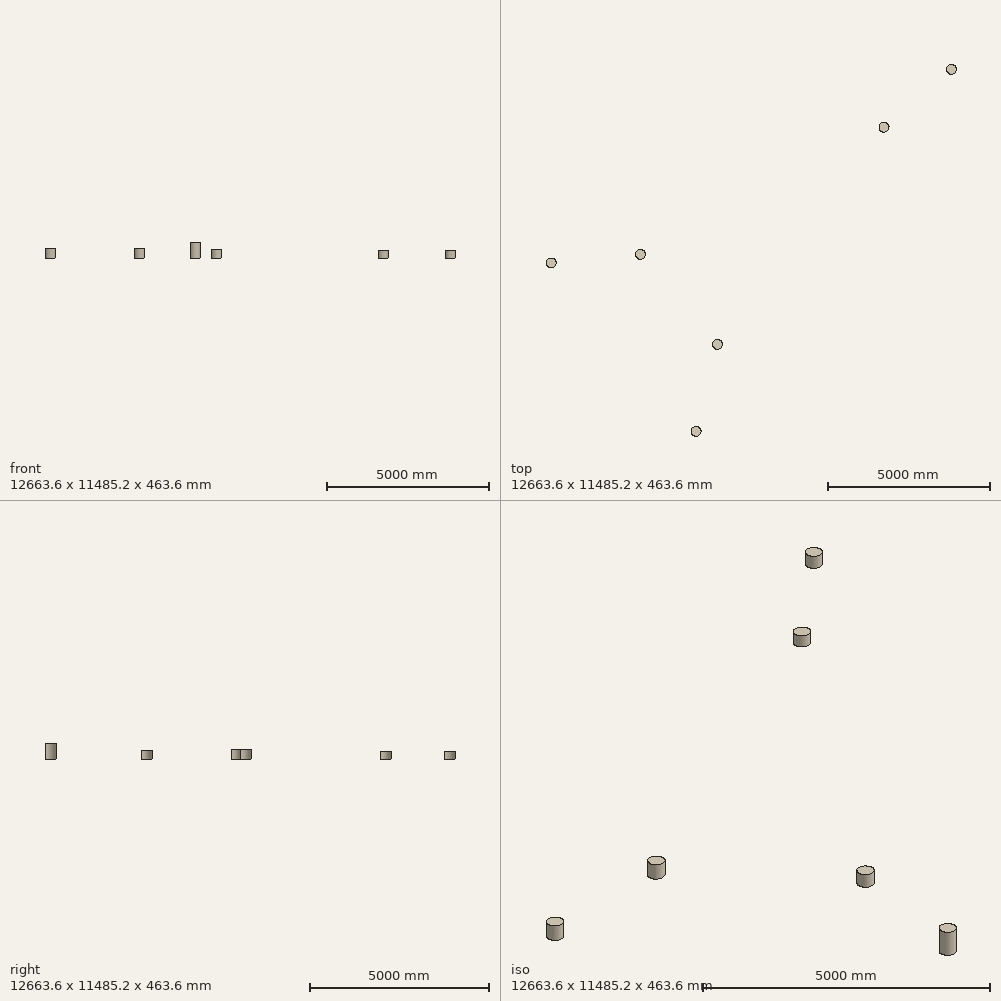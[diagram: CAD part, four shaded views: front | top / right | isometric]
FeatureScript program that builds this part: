
annotation { "Feature Type Name" : "Feature", "Feature Type Description" : "" }
export const myFeature = defineFeature(function(context is Context, id is Id, definition is map)
    precondition{}
    {
        {
            var Q0;
            Q0=qCreatedBy(makeId("Top.planeOp"),FACE);
            var sketch = newSketch(context, id + "F0", { "sketchPlane" : qUnion([Q0])});
            skLineSegment(sketch, "E0", {"start": v(5410.77, 4576.95) * mm, "end": v(-2479.54, -6603.46) * mm, "construction": true});
            skLineSegment(sketch, "E1", {"start": v(-2479.54, -6603.46) * mm, "end": v(-6948.04, -1401.09) * mm, "construction": true});
            skLineSegment(sketch, "E2", {"start": v(-6948.04, -1401.09) * mm, "end": v(5410.77, 4576.95) * mm, "construction": true});
            skLineSegment(sketch, "E3", {"start": v(5410.77, 4576.95) * mm, "end": v(-1814.73, -3915.86) * mm, "construction": true});
            skLineSegment(sketch, "E4", {"start": v(-1814.73, -3915.86) * mm, "end": v(-2479.54, -6603.46) * mm, "construction": true});
            skLineSegment(sketch, "E5", {"start": v(-1814.73, -3915.86) * mm, "end": v(-6948.04, -1401.09) * mm, "construction": true});
            skLineSegment(sketch, "E6", {"start": v(-1814.73, -3915.86) * mm, "end": v(-4192.13, -1136.3) * mm, "construction": true});
            skLineSegment(sketch, "E7", {"start": v(-4192.13, -1136.3) * mm, "end": v(-6948.04, -1401.09) * mm, "construction": true});
            skLineSegment(sketch, "E8", {"start": v(-4192.13, -1136.3) * mm, "end": v(-2479.54, -6603.46) * mm, "construction": true});
            skLineSegment(sketch, "E9", {"start": v(-4192.13, -1136.3) * mm, "end": v(3327.24, 2791.88) * mm, "construction": true});
            skLineSegment(sketch, "E10", {"start": v(3327.24, 2791.88) * mm, "end": v(-1814.73, -3915.86) * mm, "construction": true});
            skLineSegment(sketch, "E11", {"start": v(0, 0) * mm, "end": v(3327.24, 2791.88) * mm, "construction": true});
            skCircle(sketch, "E12", {"center": v(0, 0) * mm, "radius": 4343.4 * mm, "construction": true});
            skLineSegment(sketch, "E13", {"start": v(0, 0) * mm, "end": v(0, 9025.7) * mm});
            skCircle(sketch, "E14", {"center": v(0, 0) * mm, "radius": 7061.2 * mm, "construction": true});
            skCircle(sketch, "E15", {"center": v(0, 0) * mm, "radius": 4953 * mm, "construction": true});
            skLineSegment(sketch, "E16", {"start": v(3327.24, 2791.88) * mm, "end": v(4675.95, 1633.32) * mm, "construction": true});
            skLineSegment(sketch, "E17", {"start": v(4675.95, 1633.32) * mm, "end": v(4675.95, 1633.32) * mm});
            skSolve(sketch);
        }
        {
            var Q0;
            Q0=qCreatedBy(makeId("Top.planeOp"),FACE);
            var sketch = newSketch(context, id + "F1", { "sketchPlane" : qUnion([Q0])});
            skCircle(sketch, "E18", {"center": v(5410.77, 4576.95) * mm, "radius": 152.4 * mm});
            skSolve(sketch);
        }
        {
            var Q0;
            Q0=qSketchRegion(id+"F1",true);
            extrude(context, id + "F2", {"entities" : qUnion([Q0]), "depth" : 241.3 * mm});
        }
        {
            var Q0;
            Q0=qCreatedBy(makeId("Top.planeOp"),FACE);
            var sketch = newSketch(context, id + "F3", { "sketchPlane" : qUnion([Q0])});
            skCircle(sketch, "E19", {"center": v(3327.24, 2791.88) * mm, "radius": 152.4 * mm});
            skSolve(sketch);
        }
        {
            var Q0;
            Q0=qSketchRegion(id+"F3",true);
            extrude(context, id + "F4", {"entities" : qUnion([Q0]), "depth" : 219.07 * mm});
        }
        {
            var Q0;
            Q0=qCreatedBy(makeId("Top.planeOp"),FACE);
            var sketch = newSketch(context, id + "F5", { "sketchPlane" : qUnion([Q0])});
            skCircle(sketch, "E20", {"center": v(-1814.73, -3915.86) * mm, "radius": 152.4 * mm});
            skSolve(sketch);
        }
        {
            var Q0;
            Q0=qSketchRegion(id+"F5",true);
            extrude(context, id + "F6", {"entities" : qUnion([Q0]), "depth" : 254 * mm});
        }
        {
            var Q0;
            Q0=qCreatedBy(makeId("Top.planeOp"),FACE);
            var sketch = newSketch(context, id + "F7", { "sketchPlane" : qUnion([Q0])});
            skCircle(sketch, "E21", {"center": v(-4192.13, -1136.3) * mm, "radius": 152.4 * mm});
            skSolve(sketch);
        }
        {
            var Q0;
            Q0=qSketchRegion(id+"F7",true);
            extrude(context, id + "F8", {"entities" : qUnion([Q0]), "depth" : 285.75 * mm});
        }
        {
            var Q0;
            Q0=qCreatedBy(makeId("Top.planeOp"),FACE);
            var sketch = newSketch(context, id + "F9", { "sketchPlane" : qUnion([Q0])});
            skCircle(sketch, "E22", {"center": v(-6948.04, -1401.09) * mm, "radius": 152.4 * mm});
            skSolve(sketch);
        }
        {
            var Q0;
            Q0=qSketchRegion(id+"F9",true);
            extrude(context, id + "F10", {"entities" : qUnion([Q0]), "depth" : 292.1 * mm});
        }
        {
            var Q0;
            Q0=qCreatedBy(makeId("Top.planeOp"),FACE);
            var sketch = newSketch(context, id + "F11", { "sketchPlane" : qUnion([Q0])});
            skCircle(sketch, "E23", {"center": v(-2479.54, -6603.46) * mm, "radius": 152.4 * mm});
            skSolve(sketch);
        }
        {
            var Q0;
            Q0=qSketchRegion(id+"F11",true);
            extrude(context, id + "F12", {"entities" : qUnion([Q0]), "depth" : 463.55 * mm});
        }
        {
            var Q0;
            Q0=qCreatedBy(makeId("Top.planeOp"),FACE);
            var sketch = newSketch(context, id + "F13", { "sketchPlane" : qUnion([Q0])});
            skLineSegment(sketch, "E24", {"start": v(0, 0) * mm, "end": v(3327.24, 2791.88) * mm, "construction": true});
            skLineSegment(sketch, "E25", {"start": v(3327.24, 2791.88) * mm, "end": v(5410.77, 4576.95) * mm, "construction": true});
            skLineSegment(sketch, "E26", {"start": v(0, 0) * mm, "end": v(-1814.73, -3915.86) * mm, "construction": true});
            skLineSegment(sketch, "E27", {"start": v(0, 0) * mm, "end": v(-4192.13, -1136.3) * mm, "construction": true});
            skLineSegment(sketch, "E28", {"start": v(0, 0) * mm, "end": v(-2479.54, -6603.46) * mm, "construction": true});
            skLineSegment(sketch, "E29", {"start": v(0, 0) * mm, "end": v(-6948.04, -1401.09) * mm, "construction": true});
            skLineSegment(sketch, "E30", {"start": v(-1814.73, -3915.86) * mm, "end": v(-2479.54, -6603.46) * mm, "construction": true});
            skLineSegment(sketch, "E31", {"start": v(-4192.13, -1136.3) * mm, "end": v(-6948.04, -1401.09) * mm, "construction": true});
            skSolve(sketch);
        }
        {
            var Q0;
            Q0=sQuery(id+"F13.wireOp",EDGE,"E25");
            cPlane(context, id + "F14", {"entities" : qUnion([Q0]), "cplaneType" : CPlaneType.LINE_ANGLE, "offset" : 25.4 * mm, "angle" : 0 * degree, "width" : 152.4 * mm, "height" : 152.4 * mm});
        }
        {
            var Q0;
            Q0=qCreatedBy(id+"F14.planeOp",FACE);
            var sketch = newSketch(context, id + "F15", { "sketchPlane" : qUnion([Q0])});
            skLineSegment(sketch, "E32", {"start": v(-4343.17, 1174.29) * mm, "end": v(-4343.17, 219.08) * mm, "construction": true});
            skLineSegment(sketch, "E33", {"start": v(-4343.17, 219.07) * mm, "end": v(-3386.06, 5647.14) * mm});
            skLineSegment(sketch, "E34", {"start": v(-4190.77, 219.08) * mm, "end": v(-4495.57, 219.07) * mm});
            skLineSegment(sketch, "E35", {"start": v(-6934.42, 241.3) * mm, "end": v(-7239.22, 241.3) * mm});
            skLineSegment(sketch, "E36", {"start": v(-7086.82, 241.3) * mm, "end": v(-3468.12, 5583.97) * mm});
            skLineSegment(sketch, "E37", {"start": v(-3329.48, 5546.53) * mm, "end": v(-1661.5, 4733) * mm});
            skLineSegment(sketch, "E38", {"start": v(-3827.12, 3145.73) * mm, "end": v(-3714.56, 3125.88) * mm});
            skLineSegment(sketch, "E39", {"start": v(-3121.35, 5724.78) * mm, "end": v(-3148.64, 5724.78) * mm});
            skLineSegment(sketch, "E40", {"start": v(-3148.64, 5724.78) * mm, "end": v(-3148.64, 5761.55) * mm});
            skLineSegment(sketch, "E41", {"start": v(-3262.94, 5752.15) * mm, "end": v(-3237.54, 5752.15) * mm});
            skLineSegment(sketch, "E42", {"start": v(-3237.54, 5752.15) * mm, "end": v(-3237.54, 5782.18) * mm});
            skLineSegment(sketch, "E43", {"start": v(-3237.54, 5782.18) * mm, "end": v(-3262.94, 5782.18) * mm});
            skLineSegment(sketch, "E44", {"start": v(-3237.54, 5752.15) * mm, "end": v(-3237.54, 5723.7) * mm});
            skLineSegment(sketch, "E45", {"start": v(-3237.54, 5723.7) * mm, "end": v(-3266.28, 5711.98) * mm});
            skLineSegment(sketch, "E46", {"start": v(-3237.54, 5721.86) * mm, "end": v(-3237.54, 5801.23) * mm});
            skLineSegment(sketch, "E47", {"start": v(-3237.54, 5801.23) * mm, "end": v(-3148.64, 5801.23) * mm});
            skLineSegment(sketch, "E48", {"start": v(-3148.64, 5801.23) * mm, "end": v(-3148.64, 5721.86) * mm});
            skLineSegment(sketch, "E49", {"start": v(-3148.64, 5721.86) * mm, "end": v(-3237.54, 5721.86) * mm});
            skLineSegment(sketch, "E50", {"start": v(-3148.64, 5761.55) * mm, "end": v(-3148.64, 5794.88) * mm});
            skPoint(sketch, "E51", {"position": v(-3193.09, 5801.23) * mm});
            skPoint(sketch, "E52", {"position": v(-3193.09, 5721.86) * mm});
            skLineSegment(sketch, "E53.MirrorCS", {"start": v(-3350.8, 5591.09) * mm, "end": v(-3355.74, 5563.07) * mm});
            skLineSegment(sketch, "E54.MirrorCS", {"start": v(-3468.12, 5583.97) * mm, "end": v(-3443.1, 5579.56) * mm});
            skLineSegment(sketch, "E55.MirrorCS", {"start": v(-3350.8, 5591.09) * mm, "end": v(-3345.6, 5620.66) * mm});
            skLineSegment(sketch, "E56.MirrorCS", {"start": v(-3356.62, 5558.12) * mm, "end": v(-3342.28, 5639.42) * mm});
            skLineSegment(sketch, "E57.MirrorCS", {"start": v(-3429.83, 5654.86) * mm, "end": v(-3444.17, 5573.56) * mm});
            skLineSegment(sketch, "E58.MirrorCS", {"start": v(-3444.17, 5573.56) * mm, "end": v(-3356.62, 5558.12) * mm});
            skLineSegment(sketch, "E59.MirrorCS", {"start": v(-3345.6, 5620.66) * mm, "end": v(-3320.58, 5616.25) * mm});
            skLineSegment(sketch, "E60.MirrorCS", {"start": v(-3325.8, 5586.68) * mm, "end": v(-3350.8, 5591.09) * mm});
            skPoint(sketch, "E61.MirrorP", {"position": v(-3400.4, 5565.84) * mm});
            skPoint(sketch, "E62.MirrorP", {"position": v(-3386.06, 5647.14) * mm});
            skLineSegment(sketch, "E63.MirrorCS", {"start": v(-3342.28, 5639.42) * mm, "end": v(-3429.83, 5654.86) * mm});
            skLineSegment(sketch, "E64.MirrorCS", {"start": v(-3355.74, 5563.07) * mm, "end": v(-3329.48, 5546.53) * mm});
            skSolve(sketch);
        }
        {
            var Q0;
            Q0=sQuery(id+"F13.wireOp",EDGE,"E30");
            cPlane(context, id + "F16", {"entities" : qUnion([Q0]), "cplaneType" : CPlaneType.LINE_ANGLE, "offset" : 25.4 * mm, "angle" : 90 * degree, "width" : 152.4 * mm, "height" : 152.4 * mm});
        }
        {
            var Q0;
            Q0=qCreatedBy(id+"F16.planeOp",FACE);
            var sketch = newSketch(context, id + "F17", { "sketchPlane" : qUnion([Q0])});
            skLineSegment(sketch, "E65", {"start": v(-4237.06, 254) * mm, "end": v(-4237.06, 129.89) * mm, "construction": true});
            skLineSegment(sketch, "E66", {"start": v(-4237.06, 254) * mm, "end": v(-3286, 5647.67) * mm});
            skLineSegment(sketch, "E67", {"start": v(-4084.66, 254) * mm, "end": v(-4389.46, 254) * mm});
            skLineSegment(sketch, "E68", {"start": v(-6853.26, 463.55) * mm, "end": v(-7158.06, 463.55) * mm});
            skLineSegment(sketch, "E69", {"start": v(-7005.66, 463.55) * mm, "end": v(-3369.93, 5584.83) * mm});
            skLineSegment(sketch, "E70", {"start": v(-3727.07, 3146.26) * mm, "end": v(-3614.51, 3126.4) * mm});
            skLineSegment(sketch, "E71.MirrorCS", {"start": v(-3250.75, 5591.62) * mm, "end": v(-3255.7, 5563.6) * mm});
            skLineSegment(sketch, "E72.MirrorCS", {"start": v(-3369.93, 5584.83) * mm, "end": v(-3343.06, 5580.1) * mm});
            skLineSegment(sketch, "E73.MirrorCS", {"start": v(-3250.75, 5591.62) * mm, "end": v(-3245.54, 5621.19) * mm});
            skLineSegment(sketch, "E74.MirrorCS", {"start": v(-3256.57, 5558.65) * mm, "end": v(-3242.23, 5639.95) * mm});
            skLineSegment(sketch, "E75.MirrorCS", {"start": v(-3329.78, 5655.39) * mm, "end": v(-3344.12, 5574.1) * mm});
            skLineSegment(sketch, "E76.MirrorCS", {"start": v(-3344.12, 5574.1) * mm, "end": v(-3256.57, 5558.65) * mm});
            skLineSegment(sketch, "E77.MirrorCS", {"start": v(-3245.54, 5621.19) * mm, "end": v(-3220.53, 5616.78) * mm});
            skLineSegment(sketch, "E78.MirrorCS", {"start": v(-3225.74, 5587.2) * mm, "end": v(-3250.75, 5591.62) * mm});
            skPoint(sketch, "E79.MirrorP", {"position": v(-3300.34, 5566.37) * mm});
            skLineSegment(sketch, "E80.MirrorCS", {"start": v(-3242.23, 5639.95) * mm, "end": v(-3329.78, 5655.39) * mm});
            skLineSegment(sketch, "E81.MirrorCS", {"start": v(-3255.7, 5563.6) * mm, "end": v(-3229.43, 5547.06) * mm});
            skPoint(sketch, "E82", {"position": v(-3286, 5647.67) * mm});
            skSolve(sketch);
        }
        {
            var Q0;
            Q0=sQuery(id+"F13.wireOp",EDGE,"E31");
            cPlane(context, id + "F18", {"entities" : qUnion([Q0]), "cplaneType" : CPlaneType.LINE_ANGLE, "offset" : 25.4 * mm, "angle" : 0 * degree, "width" : 152.4 * mm, "height" : 152.4 * mm});
        }
        {
            var Q0;
            Q0=qCreatedBy(id+"F18.planeOp",FACE);
            var sketch = newSketch(context, id + "F19", { "sketchPlane" : qUnion([Q0])});
            skLineSegment(sketch, "E83", {"start": v(-4281.6, 1150.6) * mm, "end": v(-4281.6, 285.75) * mm, "construction": true});
            skLineSegment(sketch, "E84", {"start": v(-4281.6, 285.75) * mm, "end": v(-3336.05, 5648.15) * mm});
            skLineSegment(sketch, "E85", {"start": v(-4129.2, 285.75) * mm, "end": v(-4434, 285.75) * mm});
            skLineSegment(sketch, "E86", {"start": v(-6897.8, 292.1) * mm, "end": v(-7202.6, 292.1) * mm});
            skLineSegment(sketch, "E87", {"start": v(-7050.2, 292.1) * mm, "end": v(-3419.97, 5585.31) * mm});
            skLineSegment(sketch, "E88", {"start": v(-3777.12, 3146.74) * mm, "end": v(-3664.56, 3126.9) * mm});
            skLineSegment(sketch, "E89.MirrorCS", {"start": v(-3300.8, 5592.1) * mm, "end": v(-3305.74, 5564.08) * mm});
            skLineSegment(sketch, "E90.MirrorCS", {"start": v(-3419.97, 5585.31) * mm, "end": v(-3393.1, 5580.58) * mm});
            skLineSegment(sketch, "E91.MirrorCS", {"start": v(-3300.8, 5592.1) * mm, "end": v(-3295.59, 5621.67) * mm});
            skLineSegment(sketch, "E92.MirrorCS", {"start": v(-3306.61, 5559.14) * mm, "end": v(-3292.28, 5640.43) * mm});
            skLineSegment(sketch, "E93.MirrorCS", {"start": v(-3379.83, 5655.87) * mm, "end": v(-3394.16, 5574.57) * mm});
            skLineSegment(sketch, "E94.MirrorCS", {"start": v(-3394.16, 5574.57) * mm, "end": v(-3306.61, 5559.14) * mm});
            skLineSegment(sketch, "E95.MirrorCS", {"start": v(-3295.59, 5621.67) * mm, "end": v(-3270.57, 5617.26) * mm});
            skLineSegment(sketch, "E96.MirrorCS", {"start": v(-3275.79, 5587.7) * mm, "end": v(-3300.8, 5592.1) * mm});
            skPoint(sketch, "E97.MirrorP", {"position": v(-3350.39, 5566.86) * mm});
            skPoint(sketch, "E98.MirrorP", {"position": v(-3336.05, 5648.15) * mm});
            skLineSegment(sketch, "E99.MirrorCS", {"start": v(-3292.28, 5640.43) * mm, "end": v(-3379.83, 5655.87) * mm});
            skLineSegment(sketch, "E100.MirrorCS", {"start": v(-3305.74, 5564.08) * mm, "end": v(-3279.47, 5547.55) * mm});
            skSolve(sketch);
        }
        {
            var Q0;
            Q0=makeQuery(id+"F4.opExtrude","CAP_FACE",FACE,{"disambiguationData":[OSD([sQuery(id+"F3.wireOp",EDGE,"E19")])],"isStart":false});
            cPlane(context, id + "F20", {"entities" : qUnion([Q0]), "cplaneType" : CPlaneType.OFFSET, "offset" : 4572 * mm, "width" : 152.4 * mm, "height" : 152.4 * mm});
        }
        {
            var Q0;
            Q0=qCreatedBy(id+"F20.planeOp",FACE);
            var sketch = newSketch(context, id + "F21", { "sketchPlane" : qUnion([Q0])});
            skLineSegment(sketch, "E101", {"start": v(506.8, 1361.95) * mm, "end": v(1429.26, 262.6) * mm, "construction": true});
            skLineSegment(sketch, "E102", {"start": v(-1537.68, -96.6) * mm, "end": v(-362.15, -1497.54) * mm, "construction": true});
            skLineSegment(sketch, "E103", {"start": v(-1537.68, -96.6) * mm, "end": v(506.8, 1361.95) * mm});
            skLineSegment(sketch, "E104", {"start": v(-4323.8, 1213.17) * mm, "end": v(-4250.85, 1213.17) * mm});
            skLineSegment(sketch, "E105", {"start": v(-4250.85, 1213.17) * mm, "end": v(-4250.85, 1127.16) * mm});
            skLineSegment(sketch, "E106", {"start": v(-4250.85, 1177.9) * mm, "end": v(-4200, 1177.9) * mm});
            skLineSegment(sketch, "E107", {"start": v(-4250.85, 1152.56) * mm, "end": v(-4289.57, 1152.56) * mm});
            skLineSegment(sketch, "E108", {"start": v(-4250.85, 1192.84) * mm, "end": v(-4281.56, 1192.84) * mm});
            skLineSegment(sketch, "E109", {"start": v(506.8, 1361.95) * mm, "end": v(574.9, 1419.1) * mm});
            skLineSegment(sketch, "E110", {"start": v(574.9, 1419.1) * mm, "end": v(2077.1, 1742.9) * mm});
            skLineSegment(sketch, "E111", {"start": v(-1537.68, -96.6) * mm, "end": v(-1605.78, -153.74) * mm});
            skLineSegment(sketch, "E112", {"start": v(-1605.78, -153.74) * mm, "end": v(-2536, -1196) * mm});
            skLineSegment(sketch, "E113", {"start": v(-2536, -1196) * mm, "end": v(-2077.1, -1742.9) * mm});
            skLineSegment(sketch, "E114", {"start": v(2077.1, 1742.9) * mm, "end": v(-2077.1, -1742.9) * mm});
            skPoint(sketch, "E115", {"position": v(-949.91, -797.07) * mm});
            skPoint(sketch, "E116", {"position": v(968.03, 812.28) * mm});
            skPoint(sketch, "E117", {"position": v(0, 0) * mm});
            skSolve(sketch);
        }
        {
            var Q0;
            Q0=sQuery(id+"F21.wireOp",VERTEX,"E111.start");
            var Q1;
            Q1=sQuery(id+"F21.wireOp",EDGE,"E102");
            cPlane(context, id + "F22", {"entities" : qUnion([Q0, Q1]), "cplaneType" : CPlaneType.LINE_POINT, "offset" : 25.4 * mm, "width" : 152.4 * mm, "height" : 152.4 * mm});
        }
        {
            var Q0;
            Q0=sQuery(id+"F21.wireOp",EDGE,"E101");
            var Q1;
            Q1=sQuery(id+"F21.wireOp",VERTEX,"E101.start");
            cPlane(context, id + "F23", {"entities" : qUnion([Q0, Q1]), "cplaneType" : CPlaneType.LINE_POINT, "offset" : 25.4 * mm, "width" : 152.4 * mm, "height" : 152.4 * mm});
        }
        {
            var Q0;
            Q0=qCreatedBy(id+"F22.planeOp",FACE);
            var sketch = newSketch(context, id + "F24", { "sketchPlane" : qUnion([Q0])});
            skLineSegment(sketch, "E118", {"start": v(-1363.82, 4826.34) * mm, "end": v(-1290.87, 4826.34) * mm});
            skLineSegment(sketch, "E119", {"start": v(-1290.87, 4826.34) * mm, "end": v(-1290.87, 4740.33) * mm});
            skLineSegment(sketch, "E120", {"start": v(-1290.87, 4791.07) * mm, "end": v(-1240.02, 4791.07) * mm});
            skLineSegment(sketch, "E121", {"start": v(-1290.87, 4765.73) * mm, "end": v(-1329.59, 4765.73) * mm});
            skLineSegment(sketch, "E122", {"start": v(-1290.87, 4806) * mm, "end": v(-1321.58, 4806) * mm});
            skSolve(sketch);
        }
        {
            var Q0;
            Q0=qCreatedBy(id+"F23.planeOp",FACE);
            var sketch = newSketch(context, id + "F25", { "sketchPlane" : qUnion([Q0])});
            skLineSegment(sketch, "E123.MirrorCS", {"start": v(1387.48, 4826.34) * mm, "end": v(1314.53, 4826.34) * mm});
            skLineSegment(sketch, "E124.MirrorCS", {"start": v(1314.53, 4765.73) * mm, "end": v(1353.24, 4765.73) * mm});
            skLineSegment(sketch, "E125.MirrorCS", {"start": v(1314.53, 4826.34) * mm, "end": v(1314.53, 4740.33) * mm});
            skLineSegment(sketch, "E126.MirrorCS", {"start": v(1314.53, 4791.07) * mm, "end": v(1263.68, 4791.07) * mm});
            skLineSegment(sketch, "E127.MirrorCS", {"start": v(1314.53, 4806) * mm, "end": v(1345.24, 4806) * mm});
            skSolve(sketch);
        }
        {
            var Q0;
            Q0=sQuery(id+"F21.wireOp",EDGE,"E101");
            cPlane(context, id + "F26", {"entities" : qUnion([Q0]), "cplaneType" : CPlaneType.LINE_ANGLE, "offset" : 25.4 * mm, "angle" : 90 * degree, "width" : 152.4 * mm, "height" : 152.4 * mm});
        }
        {
            var Q0;
            Q0=qCreatedBy(id+"F26.planeOp",FACE);
            var sketch = newSketch(context, id + "F27", { "sketchPlane" : qUnion([Q0])});
            skLineSegment(sketch, "E128.0", {"start": v(717.55, 4791.07) * mm, "end": v(-717.55, 4791.07) * mm});
            skLineSegment(sketch, "E129", {"start": v(717.55, 4791.07) * mm, "end": v(615.95, 4283.07) * mm});
            skLineSegment(sketch, "E130", {"start": v(615.95, 4283.07) * mm, "end": v(-615.95, 4283.07) * mm});
            skLineSegment(sketch, "E131", {"start": v(-615.95, 4283.07) * mm, "end": v(-717.55, 4791.07) * mm});
            skLineSegment(sketch, "E132", {"start": v(0, 4791.07) * mm, "end": v(0, 4283.07) * mm, "construction": true});
            skSolve(sketch);
        }
        {
            var Q0;
            Q0=sQuery(id+"F21.wireOp",VERTEX,"E109.start");
            var Q1;
            Q1=sQuery(id+"F27.wireOp",VERTEX,"E130.start");
            var Q2;
            Q2=sQuery(id+"F24.wireOp",VERTEX,"E120.start");
            cPlane(context, id + "F28", {"entities" : qUnion([Q0, Q1, Q2]), "cplaneType" : CPlaneType.THREE_POINT, "offset" : 25.4 * mm, "width" : 152.4 * mm, "height" : 152.4 * mm});
        }
        {
            var Q0;
            Q0=qCreatedBy(makeId("Front.planeOp"),FACE);
            cPlane(context, id + "F29", {"entities" : qUnion([Q0]), "cplaneType" : CPlaneType.OFFSET, "offset" : 2540 * mm, "width" : 152.4 * mm, "height" : 152.4 * mm});
        }
        {
            var Q0;
            Q0=qCreatedBy(id+"F29.planeOp",FACE);
            var sketch = newSketch(context, id + "F30", { "sketchPlane" : qUnion([Q0])});
            skCircle(sketch, "E133", {"center": v(-759.84, -71.48) * mm, "radius": 6.54 * mm});
            skCircle(sketch, "E134", {"center": v(-759.84, -41.45) * mm, "radius": 4.95 * mm});
            skCircle(sketch, "E135", {"center": v(-763.18, -111.65) * mm, "radius": 5.08 * mm});
            skLineSegment(sketch, "E136", {"start": v(-734.44, -30.02) * mm, "end": v(-734.44, -99.93) * mm});
            skArc(sketch, "E137", {"start": v(-759.84, -30.02) * mm, "mid": v(-766.13, -31.91) * mm, "end": v(-770.34, -36.95) * mm});
            skArc(sketch, "E138", {"start": v(-774.06, -115.13) * mm, "mid": v(-769.92, -120.88) * mm, "end": v(-763.18, -123.08) * mm});
            skArc(sketch, "E139", {"start": v(-770.34, -36.95) * mm, "mid": v(-779.25, -75.7) * mm, "end": v(-774.06, -115.13) * mm});
            skLineSegment(sketch, "E140", {"start": v(-759.84, -30.02) * mm, "end": v(-734.44, -30.02) * mm});
            skArc(sketch, "E141", {"start": v(-763.18, -123.08) * mm, "mid": v(-748.14, -118.33) * mm, "end": v(-739.82, -104.94) * mm});
            skArc(sketch, "E142", {"start": v(-734.44, -99.93) * mm, "mid": v(-737.93, -101.58) * mm, "end": v(-739.82, -104.94) * mm});
            skCircle(sketch, "E143", {"center": v(-584.68, -108.37) * mm, "radius": 8.13 * mm});
            skLineSegment(sketch, "E144", {"start": v(-611.67, -38.52) * mm, "end": v(-611.67, -105.2) * mm});
            skArc(sketch, "E145", {"start": v(-606.02, -114.6) * mm, "mid": v(-577.18, -129.3) * mm, "end": v(-564.25, -99.62) * mm});
            skLineSegment(sketch, "E146", {"start": v(-585.47, -50.07) * mm, "end": v(-564.25, -99.62) * mm});
            skLineSegment(sketch, "E147", {"start": v(-611.67, -38.52) * mm, "end": v(-602.98, -38.52) * mm});
            skArc(sketch, "E148", {"start": v(-585.47, -50.07) * mm, "mid": v(-592.5, -41.67) * mm, "end": v(-602.98, -38.52) * mm});
            skLineSegment(sketch, "E149", {"start": v(-611.5, -105.2) * mm, "end": v(-611.67, -105.2) * mm});
            skArc(sketch, "E150", {"start": v(-606.74, -109.78) * mm, "mid": v(-606.5, -112.2) * mm, "end": v(-606.02, -114.6) * mm});
            skArc(sketch, "E151", {"start": v(-606.74, -109.78) * mm, "mid": v(-608.2, -106.53) * mm, "end": v(-611.5, -105.2) * mm});
            skArc(sketch, "E152", {"start": v(-420.55, -47.48) * mm, "mid": v(-433.9, -79.23) * mm, "end": v(-420.55, -110.98) * mm});
            skArc(sketch, "E153", {"start": v(-358.34, -110.98) * mm, "mid": v(-345, -79.23) * mm, "end": v(-358.34, -47.48) * mm});
            skCircle(sketch, "E154", {"center": v(-389.45, -79.23) * mm, "radius": 9.13 * mm});
            skLineSegment(sketch, "E155", {"start": v(-420.55, -110.98) * mm, "end": v(-358.34, -110.98) * mm});
            skLineSegment(sketch, "E156", {"start": v(-358.34, -47.48) * mm, "end": v(-420.55, -47.48) * mm});
            skCircle(sketch, "E157", {"center": v(676.2, -10.3) * mm, "radius": 6.54 * mm});
            skArc(sketch, "E158", {"start": v(676.2, -29.36) * mm, "mid": v(693.8, -17.6) * mm, "end": v(689.66, 3.16) * mm});
            skCircle(sketch, "E159", {"center": v(644.44, 21.44) * mm, "radius": 6.54 * mm});
            skLineSegment(sketch, "E160", {"start": v(596.82, -29.36) * mm, "end": v(600, -29.36) * mm});
            skArc(sketch, "E161", {"start": v(612.7, -29.36) * mm, "mid": v(606.34, -23) * mm, "end": v(600, -29.36) * mm});
            skLineSegment(sketch, "E162", {"start": v(689.66, 3.16) * mm, "end": v(657.91, 34.91) * mm});
            skLineSegment(sketch, "E163", {"start": v(587.3, -80.16) * mm, "end": v(438.78, -80.16) * mm});
            skLineSegment(sketch, "E164", {"start": v(438.78, -118.26) * mm, "end": v(587.3, -118.26) * mm});
            skArc(sketch, "E165", {"start": v(438.78, -80.16) * mm, "mid": v(419.73, -99.2) * mm, "end": v(438.78, -118.26) * mm});
            skCircle(sketch, "E166", {"center": v(438.78, -99.2) * mm, "radius": 6.54 * mm});
            skArc(sketch, "E167", {"start": v(625.4, -38.88) * mm, "mid": v(622.6, -32.15) * mm, "end": v(615.87, -29.36) * mm});
            skLineSegment(sketch, "E168", {"start": v(625.4, -38.88) * mm, "end": v(625.4, -42.06) * mm});
            skArc(sketch, "E169", {"start": v(587.3, -80.16) * mm, "mid": v(614.23, -69) * mm, "end": v(625.4, -42.06) * mm});
            skLineSegment(sketch, "E170", {"start": v(663.5, -38.88) * mm, "end": v(663.5, -42.06) * mm});
            skArc(sketch, "E171", {"start": v(673.02, -29.36) * mm, "mid": v(666.28, -32.15) * mm, "end": v(663.5, -38.88) * mm});
            skArc(sketch, "E172", {"start": v(587.3, -118.26) * mm, "mid": v(641.17, -95.94) * mm, "end": v(663.5, -42.06) * mm});
            skLineSegment(sketch, "E173", {"start": v(676.2, -29.36) * mm, "end": v(673.02, -29.36) * mm});
            skArc(sketch, "E174", {"start": v(593.64, -26.18) * mm, "mid": v(594.57, -28.43) * mm, "end": v(596.82, -29.36) * mm});
            skCircle(sketch, "E175", {"center": v(644.44, -10.3) * mm, "radius": 5.08 * mm});
            skLineSegment(sketch, "E176", {"start": v(612.7, -29.36) * mm, "end": v(615.87, -29.36) * mm});
            skArc(sketch, "E177", {"start": v(657.91, 34.91) * mm, "mid": v(646.65, 40.37) * mm, "end": v(634.44, 37.65) * mm});
            skLineSegment(sketch, "E178", {"start": v(593.64, -26.18) * mm, "end": v(593.64, -14.42) * mm});
            skCircle(sketch, "E179", {"center": v(600, -17.79) * mm, "radius": 1.59 * mm});
            skCircle(sketch, "E180", {"center": v(612.7, -17.79) * mm, "radius": 1.59 * mm});
            skLineSegment(sketch, "E181", {"start": v(593.64, 1.85) * mm, "end": v(593.64, -14.42) * mm});
            skLineSegment(sketch, "E182", {"start": v(602.69, 18.06) * mm, "end": v(634.44, 37.65) * mm});
            skCircle(sketch, "E183", {"center": v(-119.39, -143.82) * mm, "radius": 6.54 * mm});
            skCircle(sketch, "E184", {"center": v(-68.54, -93.07) * mm, "radius": 6.54 * mm});
            skCircle(sketch, "E185", {"center": v(-158.1, -118.42) * mm, "radius": 6.54 * mm});
            skArc(sketch, "E186", {"start": v(-71.5, -111.89) * mm, "mid": v(-50.96, -100.41) * mm, "end": v(-57.24, -77.73) * mm});
            skCircle(sketch, "E187", {"center": v(-192.33, -57.8) * mm, "radius": 6.54 * mm});
            skArc(sketch, "E188", {"start": v(-193.85, -38.82) * mm, "mid": v(-210.69, -52.71) * mm, "end": v(-203.42, -73.3) * mm});
            skArc(sketch, "E189", {"start": v(-71.5, -111.89) * mm, "mid": v(-93.4, -119) * mm, "end": v(-100.56, -140.89) * mm});
            skLineSegment(sketch, "E190", {"start": v(-177.84, -91.61) * mm, "end": v(-203.42, -73.3) * mm});
            skCircle(sketch, "E191", {"center": v(-150.1, -78.14) * mm, "radius": 5.08 * mm});
            skCircle(sketch, "E192", {"center": v(-119.34, -93.02) * mm, "radius": 5.08 * mm});
            skArc(sketch, "E193", {"start": v(-174.38, -108.53) * mm, "mid": v(-173.48, -129.65) * mm, "end": v(-153.64, -136.94) * mm});
            skArc(sketch, "E194", {"start": v(-138.15, -147.1) * mm, "mid": v(-116.28, -162.61) * mm, "end": v(-100.56, -140.89) * mm});
            skArc(sketch, "E195", {"start": v(-138.15, -147.1) * mm, "mid": v(-143.7, -138.67) * mm, "end": v(-153.64, -136.94) * mm});
            skArc(sketch, "E196", {"start": v(-174.38, -108.53) * mm, "mid": v(-172.8, -99.4) * mm, "end": v(-177.84, -91.61) * mm});
            skCircle(sketch, "E197", {"center": v(222, -97.76) * mm, "radius": 44.45 * mm});
            skArc(sketch, "E198", {"start": v(-57.24, -77.73) * mm, "mid": v(-122.03, -45.95) * mm, "end": v(-193.85, -38.82) * mm});
            skArc(sketch, "E199", {"start": v(602.69, 18.06) * mm, "mid": v(596.06, 11.13) * mm, "end": v(593.64, 1.85) * mm});
            skCircle(sketch, "E200", {"center": v(612.7, 1.85) * mm, "radius": 6.54 * mm});
            skLineSegment(sketch, "E201", {"start": v(865.88, 148.21) * mm, "end": v(112.57, 148.21) * mm});
            skLineSegment(sketch, "E202", {"start": v(112.57, 148.21) * mm, "end": v(112.57, -255.43) * mm});
            skLineSegment(sketch, "E203", {"start": v(112.57, -255.43) * mm, "end": v(865.88, -255.43) * mm});
            skLineSegment(sketch, "E204", {"start": v(865.88, -255.43) * mm, "end": v(865.88, 148.21) * mm});
            skLineSegment(sketch, "E205", {"start": v(19.99, 148.21) * mm, "end": v(-865.88, 148.21) * mm});
            skLineSegment(sketch, "E206", {"start": v(-865.88, 148.21) * mm, "end": v(-865.88, -259.63) * mm});
            skLineSegment(sketch, "E207", {"start": v(-865.88, -259.63) * mm, "end": v(19.99, -259.63) * mm});
            skLineSegment(sketch, "E208", {"start": v(19.99, -259.63) * mm, "end": v(19.99, 148.21) * mm});
            skSolve(sketch);
        }
        {
            var Q0;
            Q0=qCreatedBy(id+"F28.planeOp",FACE);
            var sketch = newSketch(context, id + "F31", { "sketchPlane" : qUnion([Q0])});
            skLineSegment(sketch, "E209", {"start": v(-2010.66, 4573.13) * mm, "end": v(-1948.28, 4197.27) * mm});
            skLineSegment(sketch, "E210", {"start": v(576.83, 4936.08) * mm, "end": v(604.4, 4482.9) * mm});
            skLineSegment(sketch, "E211", {"start": v(-1948.28, 4197.27) * mm, "end": v(-1943.08, 4165.95) * mm});
            skLineSegment(sketch, "E212", {"start": v(-1943.08, 4165.95) * mm, "end": v(-1911.76, 4171.15) * mm});
            skLineSegment(sketch, "E213", {"start": v(-1943.08, 4165.95) * mm, "end": v(-1976.4, 4172.74) * mm});
            skLineSegment(sketch, "E214", {"start": v(-1943.08, 4165.95) * mm, "end": v(-2131.42, 4044.58) * mm});
            skLineSegment(sketch, "E215", {"start": v(-1977.97, 4143.47) * mm, "end": v(-1977.97, 4140.87) * mm});
            skLineSegment(sketch, "E216.MirrorCS", {"start": v(606.32, 4451.2) * mm, "end": v(637.28, 4465.26) * mm});
            skLineSegment(sketch, "E217.MirrorCS", {"start": v(645.35, 4437.08) * mm, "end": v(645.35, 4434.5) * mm});
            skLineSegment(sketch, "E218.MirrorCS", {"start": v(604.4, 4482.9) * mm, "end": v(606.32, 4451.2) * mm});
            skLineSegment(sketch, "E219.MirrorCS", {"start": v(606.32, 4451.2) * mm, "end": v(574.63, 4449.27) * mm});
            skLineSegment(sketch, "E220.MirrorCS", {"start": v(606.32, 4451.2) * mm, "end": v(817, 4374.95) * mm});
            skLineSegment(sketch, "E221", {"start": v(574.63, 4449.27) * mm, "end": v(-1911.76, 4171.15) * mm});
            skLineSegment(sketch, "E222", {"start": v(519.83, 4977.58) * mm, "end": v(-1967.45, 4630.2) * mm});
            skLineSegment(sketch, "E223", {"start": v(576.83, 4936.08) * mm, "end": v(-1911.76, 4171.15) * mm, "construction": true});
            skLineSegment(sketch, "E224", {"start": v(-2010.66, 4573.13) * mm, "end": v(574.63, 4449.27) * mm, "construction": true});
            skSolve(sketch);
        }
        {
            var Q0;
            Q0=sQuery(id+"F19.wireOp",EDGE,"E99.MirrorCS");
            cPoint(context, id + "F32", {"entities" : qUnion([Q0]), "parameter" : 0.5});
        }
        {
            var Q0;
            Q0=sQuery(id+"F24.wireOp",VERTEX,"E119.start");
            var Q1;
            Q1=qCreatedBy(id+"F32",VERTEX);
            var Q2;
            Q2=sQuery(id+"F19.wireOp",VERTEX,"E97.MirrorP");
            cPlane(context, id + "F33", {"entities" : qUnion([Q0, Q1, Q2]), "cplaneType" : CPlaneType.THREE_POINT, "offset" : 25.4 * mm, "width" : 152.4 * mm, "height" : 152.4 * mm});
        }
        {
            var Q0;
            Q0=qCreatedBy(id+"F33.planeOp",FACE);
            var sketch = newSketch(context, id + "F34", { "sketchPlane" : qUnion([Q0])});
            skLineSegment(sketch, "E225.0", {"start": v(1374.42, 4826.37) * mm, "end": v(1303.39, 4822.96) * mm});
            skLineSegment(sketch, "E226.0", {"start": v(3129.02, 5648.55) * mm, "end": v(3152.14, 5653.12) * mm});
            skLineSegment(sketch, "E227.0", {"start": v(3158.64, 5620.28) * mm, "end": v(3142.62, 5701.26) * mm});
            skLineSegment(sketch, "E228", {"start": v(3129.02, 5648.55) * mm, "end": v(1374.42, 4826.37) * mm});
            skSolve(sketch);
        }
        {
            var Q0;
            Q0=sQuery(id+"F19.wireOp",VERTEX,"E88.start");
            var Q1;
            Q1=sQuery(id+"F19.wireOp",VERTEX,"E97.MirrorP");
            var Q2;
            Q2=sQuery(id+"F31.wireOp",VERTEX,"E214.start");
            cPlane(context, id + "F35", {"entities" : qUnion([Q0, Q1, Q2]), "cplaneType" : CPlaneType.THREE_POINT, "offset" : 25.4 * mm, "width" : 152.4 * mm, "height" : 152.4 * mm});
        }
        {
            var Q0;
            Q0=qCreatedBy(id+"F35.planeOp",FACE);
            var sketch = newSketch(context, id + "F36", { "sketchPlane" : qUnion([Q0])});
            skLineSegment(sketch, "E229.0", {"start": v(-1358.58, 4341.55) * mm, "end": v(-1556.1, 4257.56) * mm});
            skLineSegment(sketch, "E230.0", {"start": v(-3736.41, 3207.1) * mm, "end": v(-3630.09, 3186.63) * mm});
            skLineSegment(sketch, "E231", {"start": v(-1556.1, 4257.56) * mm, "end": v(-3630.09, 3186.63) * mm});
            skSolve(sketch);
        }
        {
            var Q0;
            Q0=sQuery(id+"F15.wireOp",VERTEX,"E38.start");
            var Q1;
            Q1=sQuery(id+"F15.wireOp",VERTEX,"E61.MirrorP");
            var Q2;
            Q2=sQuery(id+"F31.wireOp",VERTEX,"E219.MirrorCS.start");
            cPlane(context, id + "F37", {"entities" : qUnion([Q0, Q1, Q2]), "cplaneType" : CPlaneType.THREE_POINT, "offset" : 25.4 * mm, "width" : 152.4 * mm, "height" : 152.4 * mm});
        }
        {
            var Q0;
            Q0=qCreatedBy(id+"F37.planeOp",FACE);
            var sketch = newSketch(context, id + "F38", { "sketchPlane" : qUnion([Q0])});
            skLineSegment(sketch, "E232.0", {"start": v(-1163.58, 4196.43) * mm, "end": v(-1359.81, 4088.8) * mm});
            skLineSegment(sketch, "E233.0", {"start": v(-3770.36, 3015.35) * mm, "end": v(-3661.41, 2999.3) * mm});
            skLineSegment(sketch, "E234", {"start": v(-1359.81, 4088.8) * mm, "end": v(-3661.41, 2999.3) * mm});
            skSolve(sketch);
        }
        {
            var Q0;
            Q0=sQuery(id+"F38.wireOp",VERTEX,"E233.0.start");
            var Q1;
            Q1=sQuery(id+"F15.wireOp",VERTEX,"E61.MirrorP");
            var Q2;
            Q2=sQuery(id+"F21.wireOp",VERTEX,"E109.end");
            cPlane(context, id + "F39", {"entities" : qUnion([Q0, Q1, Q2]), "cplaneType" : CPlaneType.THREE_POINT, "offset" : 25.4 * mm, "width" : 152.4 * mm, "height" : 152.4 * mm});
        }
        {
            var Q0;
            Q0=qCreatedBy(id+"F39.planeOp",FACE);
            var sketch = newSketch(context, id + "F40", { "sketchPlane" : qUnion([Q0])});
            skLineSegment(sketch, "E235.0", {"start": v(-1197.99, 4728.5) * mm, "end": v(-1128.8, 4731.38) * mm});
            skLineSegment(sketch, "E236.0", {"start": v(-3284.02, 5445.04) * mm, "end": v(-3307.76, 5448.44) * mm});
            skLineSegment(sketch, "E237", {"start": v(-3284.02, 5445.04) * mm, "end": v(-1197.99, 4728.5) * mm});
            skSolve(sketch);
        }
        {
            var Q0;
            Q0=sQuery(id+"F17.wireOp",VERTEX,"E82");
            var Q1;
            Q1=sQuery(id+"F17.wireOp",VERTEX,"E70.start");
            var Q2;
            Q2=sQuery(id+"F21.wireOp",VERTEX,"E102.end");
            cPlane(context, id + "F41", {"entities" : qUnion([Q0, Q1, Q2]), "cplaneType" : CPlaneType.THREE_POINT, "offset" : 25.4 * mm, "width" : 152.4 * mm, "height" : 152.4 * mm});
        }
        {
            var Q0;
            Q0=qCreatedBy(id+"F41.planeOp",FACE);
            var sketch = newSketch(context, id + "F42", { "sketchPlane" : qUnion([Q0])});
            skLineSegment(sketch, "E238", {"start": v(1150.44, 4804.31) * mm, "end": v(1201.12, 4807.85) * mm});
            skLineSegment(sketch, "E239", {"start": v(1201.12, 4807.85) * mm, "end": v(1198.68, 4842.81) * mm});
            skLineSegment(sketch, "E240", {"start": v(1198.68, 4842.81) * mm, "end": v(1271.4, 4847.89) * mm});
            skLineSegment(sketch, "E241.0", {"start": v(2980.67, 5704.64) * mm, "end": v(3003.35, 5709.57) * mm});
            skLineSegment(sketch, "E242", {"start": v(2980.67, 5704.64) * mm, "end": v(1271.4, 4847.89) * mm});
            skSolve(sketch);
        }
        {
            var Q0;
            Q0=sQuery(id+"F17.wireOp",EDGE,"E80.MirrorCS");
            cPoint(context, id + "F43", {"entities" : qUnion([Q0]), "parameter" : 0.5});
        }
        {
            var Q0;
            Q0 = qCreatedBy(id + "F43" ,VERTEX);
            var Q1;
            Q1=sQuery(id+"F17.wireOp",VERTEX,"E79.MirrorP");
            var Q2;
            Q2=sQuery(id+"F19.wireOp",VERTEX,"E98.MirrorP");
            cPlane(context, id + "F44", {"entities" : qUnion([Q0, Q1, Q2]), "cplaneType" : CPlaneType.THREE_POINT, "offset" : 25.4 * mm, "width" : 152.4 * mm, "height" : 152.4 * mm});
        }
        {
            var Q0;
            Q0=qCreatedBy(id+"F44.planeOp",FACE);
            var sketch = newSketch(context, id + "F45", { "sketchPlane" : qUnion([Q0])});
            skPoint(sketch, "E243.0", {"position": v(-1901.82, 4898.8) * mm});
            skPoint(sketch, "E244.0", {"position": v(600.51, 5202.06) * mm});
            skLineSegment(sketch, "E245", {"start": v(-1927.08, 4898.28) * mm, "end": v(-1857.25, 4899.74) * mm});
            skLineSegment(sketch, "E246", {"start": v(625.48, 5207.7) * mm, "end": v(557.35, 5192.31) * mm});
            skLineSegment(sketch, "E247", {"start": v(-1857.25, 4899.74) * mm, "end": v(557.35, 5192.31) * mm});
            skSolve(sketch);
        }
        {
            var Q0;
            Q0=sQuery(id+"F19.wireOp",VERTEX,"E98.MirrorP");
            var Q1;
            Q1=sQuery(id+"F36.wireOp",VERTEX,"E230.0.start");
            var Q2;
            Q2=sQuery(id+"F15.wireOp",VERTEX,"E62.MirrorP");
            cPlane(context, id + "F46", {"entities" : qUnion([Q0, Q1, Q2]), "cplaneType" : CPlaneType.THREE_POINT, "offset" : 25.4 * mm, "width" : 152.4 * mm, "height" : 152.4 * mm});
        }
        {
            var Q0;
            Q0=sQuery(id+"F15.wireOp",VERTEX,"E62.MirrorP");
            var Q1;
            Q1=sQuery(id+"F15.wireOp",VERTEX,"E61.MirrorP");
            var Q2;
            Q2=sQuery(id+"F17.wireOp",VERTEX,"E79.MirrorP");
            cPlane(context, id + "F47", {"entities" : qUnion([Q0, Q1, Q2]), "cplaneType" : CPlaneType.THREE_POINT, "offset" : 25.4 * mm, "width" : 152.4 * mm, "height" : 152.4 * mm});
        }
        {
            var Q0;
            Q0=sQuery(id+"F27.wireOp",VERTEX,"E131.end");
            var Q1;
            Q1=sQuery(id+"F27.wireOp",VERTEX,"E131.start");
            var Q2;
            Q2=sQuery(id+"F42.wireOp",VERTEX,"E239.start");
            cPlane(context, id + "F48", {"entities" : qUnion([Q0, Q1, Q2]), "cplaneType" : CPlaneType.THREE_POINT, "offset" : 25.4 * mm, "width" : 152.4 * mm, "height" : 152.4 * mm});
        }
        {
            var Q0;
            Q0=qCreatedBy(id+"F48.planeOp",FACE);
            var sketch = newSketch(context, id + "F49", { "sketchPlane" : qUnion([Q0])});
            skLineSegment(sketch, "E248", {"start": v(-414.34, 5029.06) * mm, "end": v(-498.57, 4606.86) * mm});
            skLineSegment(sketch, "E249", {"start": v(-498.57, 4606.86) * mm, "end": v(-504.79, 4575.72) * mm});
            skLineSegment(sketch, "E250", {"start": v(-504.79, 4575.72) * mm, "end": v(-473.65, 4569.5) * mm});
            skLineSegment(sketch, "E251", {"start": v(-504.79, 4575.72) * mm, "end": v(-533.54, 4593.85) * mm});
            skLineSegment(sketch, "E252", {"start": v(-504.79, 4575.72) * mm, "end": v(-723.87, 4528.78) * mm});
            skLineSegment(sketch, "E253", {"start": v(-545.37, 4567.02) * mm, "end": v(-545.37, 4564.44) * mm});
            skSolve(sketch);
        }
        {
            var Q0;
            Q0=sQuery(id+"F49.wireOp",VERTEX,"E252.start");
            var Q1;
            Q1=sQuery(id+"F17.wireOp",VERTEX,"E70.start");
            var Q2;
            Q2=sQuery(id+"F17.wireOp",VERTEX,"E79.MirrorP");
            cPlane(context, id + "F50", {"entities" : qUnion([Q0, Q1, Q2]), "cplaneType" : CPlaneType.THREE_POINT, "offset" : 25.4 * mm, "width" : 152.4 * mm, "height" : 152.4 * mm});
        }
        {
            var Q0;
            Q0=qCreatedBy(id+"F50.planeOp",FACE);
            var sketch = newSketch(context, id + "F51", { "sketchPlane" : qUnion([Q0])});
            skLineSegment(sketch, "E254.0", {"start": v(-3648.4, 3262.52) * mm, "end": v(-3543.65, 3240.73) * mm});
            skLineSegment(sketch, "E255.0", {"start": v(-1298.55, 4360.53) * mm, "end": v(-1500.79, 4286.53) * mm});
            skLineSegment(sketch, "E256", {"start": v(-1500.79, 4286.53) * mm, "end": v(-3543.65, 3240.73) * mm});
            skSolve(sketch);
        }
        {
            var Q0;
            Q0=sQuery(id+"F17.wireOp",VERTEX,"E82");
            var Q1;
            Q1=sQuery(id+"F17.wireOp",EDGE,"E66");
            cPlane(context, id + "F52", {"entities" : qUnion([Q0, Q1]), "cplaneType" : CPlaneType.LINE_POINT, "offset" : 25.4 * mm, "width" : 152.4 * mm, "height" : 152.4 * mm});
        }
        {
            var Q0;
            Q0=qCreatedBy(makeId("Top.planeOp"),FACE);
            cPlane(context, id + "F53", {"entities" : qUnion([Q0]), "cplaneType" : CPlaneType.OFFSET, "offset" : 6096 * mm, "width" : 152.4 * mm, "height" : 152.4 * mm});
        }
        {
            var Q0;
            Q0=sQuery(id+"F15.wireOp",VERTEX,"E60.MirrorCS.start");
            var Q1;
            Q1=sQuery(id+"F19.wireOp",VERTEX,"E97.MirrorP");
            var Q2;
            Q2=sQuery(id+"F19.wireOp",VERTEX,"E83.end");
            cPlane(context, id + "F54", {"entities" : qUnion([Q0, Q1, Q2]), "cplaneType" : CPlaneType.THREE_POINT, "offset" : 25.4 * mm, "width" : 152.4 * mm, "height" : 152.4 * mm});
        }
        {
            var Q0;
            Q0=sQuery(id+"F0.wireOp",VERTEX,"E16.end");
            var Q1;
            Q1=sQuery(id+"F0.wireOp",VERTEX,"E16.start");
            var Q2;
            Q2=sQuery(id+"F15.wireOp",VERTEX,"E64.MirrorCS.end");
            cPlane(context, id + "F58", {"entities" : qUnion([Q0, Q1, Q2]), "cplaneType" : CPlaneType.THREE_POINT, "offset" : 25.4 * mm, "width" : 152.4 * mm, "height" : 152.4 * mm});
        }
        {
            var Q0;
            Q0=sQuery(id+"F15.wireOp",VERTEX,"E61.MirrorP");
            var Q1;
            Q1=sQuery(id+"F15.wireOp",VERTEX,"E62.MirrorP");
            var Q2;
            Q2=sQuery(id+"F25.wireOp",VERTEX,"E125.MirrorCS.start");
            cPlane(context, id + "F55", {"entities" : qUnion([Q0, Q1, Q2]), "cplaneType" : CPlaneType.THREE_POINT, "offset" : 25.4 * mm, "width" : 152.4 * mm, "height" : 152.4 * mm});
        }
    });
